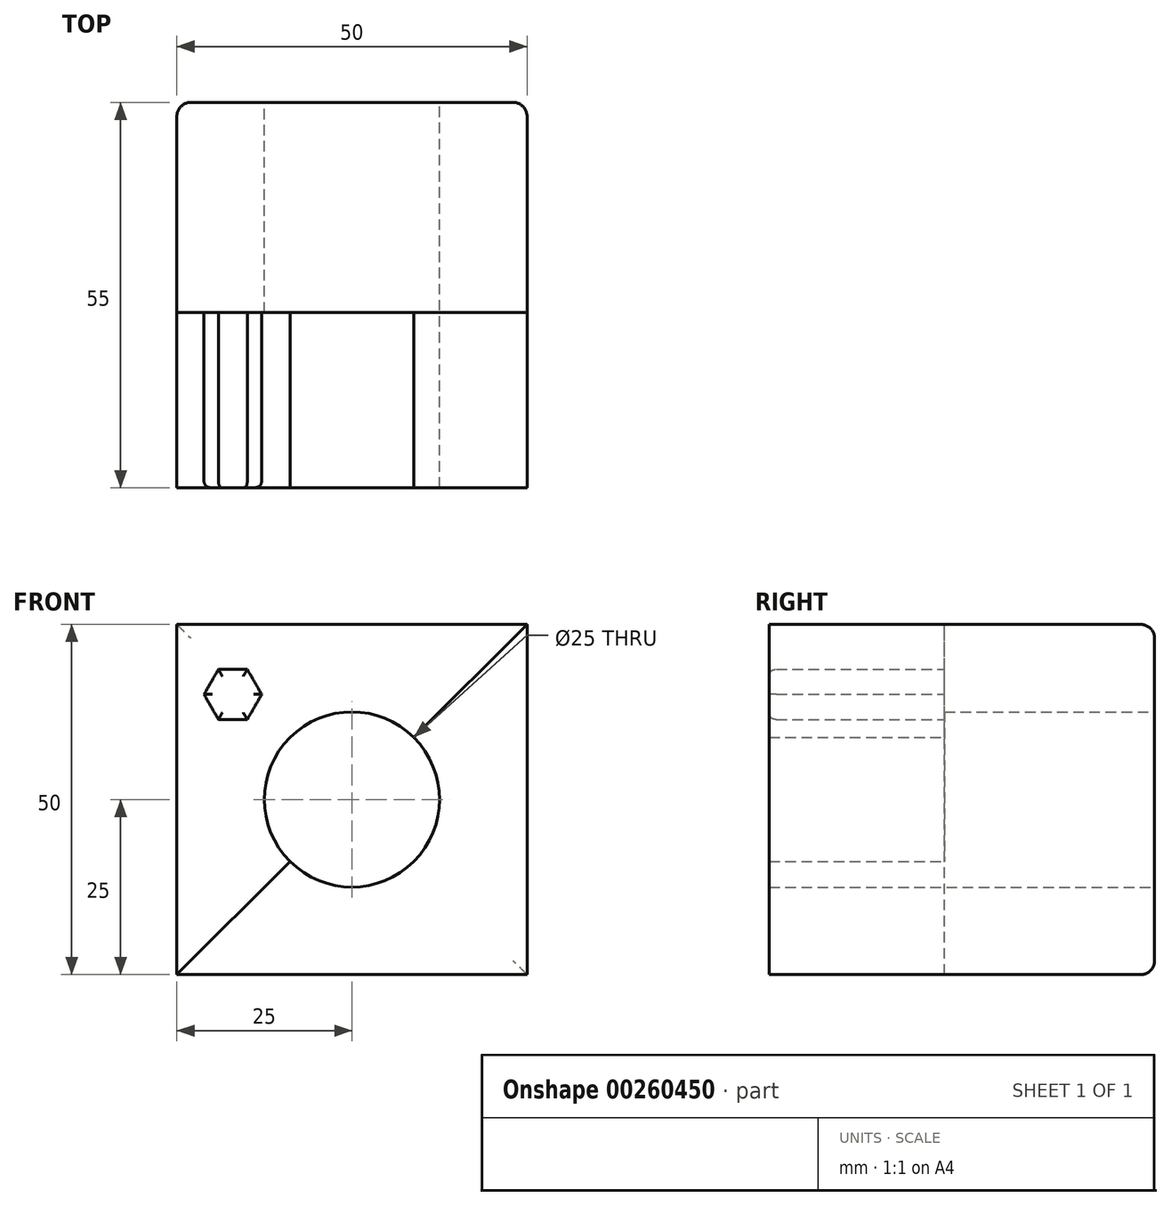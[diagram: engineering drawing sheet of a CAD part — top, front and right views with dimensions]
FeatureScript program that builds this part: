
annotation { "Feature Type Name" : "Feature", "Feature Type Description" : "" }
export const myFeature = defineFeature(function(context is Context, id is Id, definition is map)
    precondition{}
    {
        {
            var Q0;
            Q0=qCreatedBy(makeId("Front.planeOp"),FACE);
            var sketch = newSketch(context, id + "F0", { "sketchPlane" : qUnion([Q0])});
            skLineSegment(sketch, "E0", {"start": v(-25, 25) * mm, "end": v(25, 25) * mm});
            skLineSegment(sketch, "E1", {"start": v(25, 25) * mm, "end": v(25, -25) * mm});
            skLineSegment(sketch, "E2", {"start": v(25, -25) * mm, "end": v(-25, -25) * mm});
            skLineSegment(sketch, "E3", {"start": v(-25, -25) * mm, "end": v(-25, 25) * mm});
            skCircle(sketch, "E4", {"center": v(0, 0) * mm, "radius": 12.5 * mm});
            skSolve(sketch);
        }
        {
            var Q0;
            Q0 = qSketchRegion(id + "F0", true);
            extrude(context, id + "F1", {"entities" : qUnion([Q0]), "depth" : 30 * mm});
        }
        {
            var Q0;
            Q0 = qSketchRegion(id + "F0", true);
            extrude(context, id + "F2", {"entities" : qUnion([Q0]), "operationType" : NewBodyOperationType.ADD, "depth" : 25 * mm});
        }
        {
            var Q0;
            Q0=makeQuery(id+"F1.opExtrude","CAP_FACE",FACE,{"disambiguationData":[OSD([sQuery(id+"F0.wireOp",EDGE,"E0"),sQuery(id+"F0.wireOp",EDGE,"E1"),sQuery(id+"F0.wireOp",EDGE,"E2"),sQuery(id+"F0.wireOp",EDGE,"E3"),sQuery(id+"F0.wireOp",EDGE,"E4")])],"isStart":false});
            var sketch = newSketch(context, id + "F3", { "sketchPlane" : qUnion([Q0])});
            skLineSegment(sketch, "E5", {"start": v(-25, -25) * mm, "end": v(-8.84, -8.84) * mm});
            skArc(sketch, "E6", {"start": v(-8.84, -8.84) * mm, "mid": v(8.84, -8.84) * mm, "end": v(8.84, 8.84) * mm});
            skLineSegment(sketch, "E7.trimOffspring", {"start": v(8.84, 8.84) * mm, "end": v(25, 25) * mm});
            skLineSegment(sketch, "E8", {"start": v(-25, -25) * mm, "end": v(25, -25) * mm});
            skLineSegment(sketch, "E9", {"start": v(25, 25) * mm, "end": v(25, -25) * mm});
            skSolve(sketch);
        }
        {
            var Q0;
            Q0 = qSketchRegion(id + "F3", true);
            extrude(context, id + "F4", {"entities" : qUnion([Q0]), "operationType" : NewBodyOperationType.ADD, "depth" : 25 * mm});
        }
        {
            var Q0;
            Q0=makeQuery(id+"F4.opExtrude","SWEPT_FACE",FACE,{"disambiguationData":[OSD([sQuery(id+"F3.wireOp",EDGE,"E5")])]});
            var sketch = newSketch(context, id + "F5", { "sketchPlane" : qUnion([Q0])});
            skCircle(sketch, "E10.cCircle", {"center": v(-23.93, -43) * mm, "radius": 6 * mm, "construction": true});
            skPoint(sketch, "E10.cCircle.centerSnap0", {"position": v(-23.93, -30) * mm});
            skLineSegment(sketch, "E10.0", {"start": v(-34.32, -49) * mm, "end": v(-23.93, -31) * mm});
            skLineSegment(sketch, "E10.1", {"start": v(-23.93, -31) * mm, "end": v(-13.54, -49) * mm});
            skLineSegment(sketch, "E10.2", {"start": v(-13.54, -49) * mm, "end": v(-34.32, -49) * mm});
            skPoint(sketch, "E10.0.midPoint", {"position": v(-29.12, -40) * mm});
            skCircle(sketch, "E11.cCircle", {"center": v(23.36, -43) * mm, "radius": 7.38 * mm, "construction": true});
            skLineSegment(sketch, "E11.0", {"start": v(14.83, -42.82) * mm, "end": v(19.25, -35.53) * mm});
            skLineSegment(sketch, "E11.1", {"start": v(19.25, -35.53) * mm, "end": v(27.77, -35.7) * mm});
            skLineSegment(sketch, "E11.2", {"start": v(27.77, -35.7) * mm, "end": v(31.88, -43.18) * mm});
            skLineSegment(sketch, "E11.3", {"start": v(31.88, -43.18) * mm, "end": v(27.46, -50.47) * mm});
            skLineSegment(sketch, "E11.4", {"start": v(27.46, -50.47) * mm, "end": v(18.94, -50.3) * mm});
            skLineSegment(sketch, "E11.5", {"start": v(18.94, -50.3) * mm, "end": v(14.83, -42.82) * mm});
            skPoint(sketch, "E11.0.midPoint", {"position": v(17.04, -39.17) * mm});
            skSolve(sketch);
        }
        {
            var Q0;
            Q0 = qSketchRegion(id + "F5", true);
            extrude(context, id + "F6", {"entities" : qUnion([Q0]), "operationType" : NewBodyOperationType.REMOVE, "oppositeDirection" : true, "depth" : 50 * mm});
        }
        {
            var Q0;
            Q0=makeQuery(id+"F1.opExtrude","CAP_FACE",FACE,{"disambiguationData":[OSD([sQuery(id+"F0.wireOp",EDGE,"E0"),sQuery(id+"F0.wireOp",EDGE,"E1"),sQuery(id+"F0.wireOp",EDGE,"E2"),sQuery(id+"F0.wireOp",EDGE,"E3"),sQuery(id+"F0.wireOp",EDGE,"E4")])],"isStart":false});
            var sketch = newSketch(context, id + "F7", { "sketchPlane" : qUnion([Q0])});
            skCircle(sketch, "E12.cCircle", {"center": v(-17, 15) * mm, "radius": 3.57 * mm, "construction": true});
            skLineSegment(sketch, "E12.0", {"start": v(-14.94, 11.43) * mm, "end": v(-19.06, 11.43) * mm});
            skLineSegment(sketch, "E12.1", {"start": v(-19.06, 11.43) * mm, "end": v(-21.12, 15) * mm});
            skLineSegment(sketch, "E12.2", {"start": v(-21.12, 15) * mm, "end": v(-19.06, 18.57) * mm});
            skLineSegment(sketch, "E12.3", {"start": v(-19.06, 18.57) * mm, "end": v(-14.94, 18.57) * mm});
            skLineSegment(sketch, "E12.4", {"start": v(-14.94, 18.57) * mm, "end": v(-12.88, 15) * mm});
            skLineSegment(sketch, "E12.5", {"start": v(-12.88, 15) * mm, "end": v(-14.94, 11.43) * mm});
            skPoint(sketch, "E12.0.midPoint", {"position": v(-17, 11.43) * mm});
            skSolve(sketch);
        }
        {
            var Q0;
            Q0 = qSketchRegion(id + "F7", true);
            extrude(context, id + "F8", {"entities" : qUnion([Q0]), "operationType" : NewBodyOperationType.ADD, "depth" : 25 * mm});
        }
        {
            var Q0;
            Q0=makeQuery(id+"F8.opExtrude","CAP_EDGE",EDGE,{"disambiguationData":[OSD([sQuery(id+"F7.wireOp",EDGE,"E12.2")])],"isStart":false});
            var Q1;
            Q1=makeQuery(id+"F8.opExtrude","CAP_EDGE",EDGE,{"disambiguationData":[OSD([sQuery(id+"F7.wireOp",EDGE,"E12.1")])],"isStart":false});
            var Q2;
            Q2=makeQuery(id+"F8.opExtrude","CAP_EDGE",EDGE,{"disambiguationData":[OSD([sQuery(id+"F7.wireOp",EDGE,"E12.0")])],"isStart":false});
            var Q3;
            Q3=makeQuery(id+"F8.opExtrude","CAP_EDGE",EDGE,{"disambiguationData":[OSD([sQuery(id+"F7.wireOp",EDGE,"E12.5")])],"isStart":false});
            var Q4;
            Q4=makeQuery(id+"F8.opExtrude","CAP_EDGE",EDGE,{"disambiguationData":[OSD([sQuery(id+"F7.wireOp",EDGE,"E12.4")])],"isStart":false});
            var Q5;
            Q5=makeQuery(id+"F8.opExtrude","CAP_EDGE",EDGE,{"disambiguationData":[OSD([sQuery(id+"F7.wireOp",EDGE,"E12.3")])],"isStart":false});
            fillet(context, id + "F9", {"entities" : qUnion([Q0, Q1, Q2, Q3, Q4, Q5]), "radius" : 1 * mm, "tangentPropagation" : true, "rho" : 0.5, "crossSection" : FilletCrossSection.CONIC, "allowEdgeOverflow" : false});
        }
        {
            var Q0;
            Q0=makeQuery(id+"F1.opExtrude","CAP_EDGE",EDGE,{"disambiguationData":[OSD([sQuery(id+"F0.wireOp",EDGE,"E1")])],"isStart":true});
            var Q1;
            Q1=makeQuery(id+"F1.opExtrude","CAP_EDGE",EDGE,{"disambiguationData":[OSD([sQuery(id+"F0.wireOp",EDGE,"E2")])],"isStart":true});
            var Q2;
            Q2=makeQuery(id+"F1.opExtrude","CAP_EDGE",EDGE,{"disambiguationData":[OSD([sQuery(id+"F0.wireOp",EDGE,"E3")])],"isStart":true});
            var Q3;
            Q3=makeQuery(id+"F1.opExtrude","CAP_EDGE",EDGE,{"disambiguationData":[OSD([sQuery(id+"F0.wireOp",EDGE,"E0")])],"isStart":true});
            fillet(context, id + "F10", {"entities" : qUnion([Q0, Q1, Q2, Q3]), "radius" : 2 * mm, "tangentPropagation" : true, "allowEdgeOverflow" : false});
        }
    });
